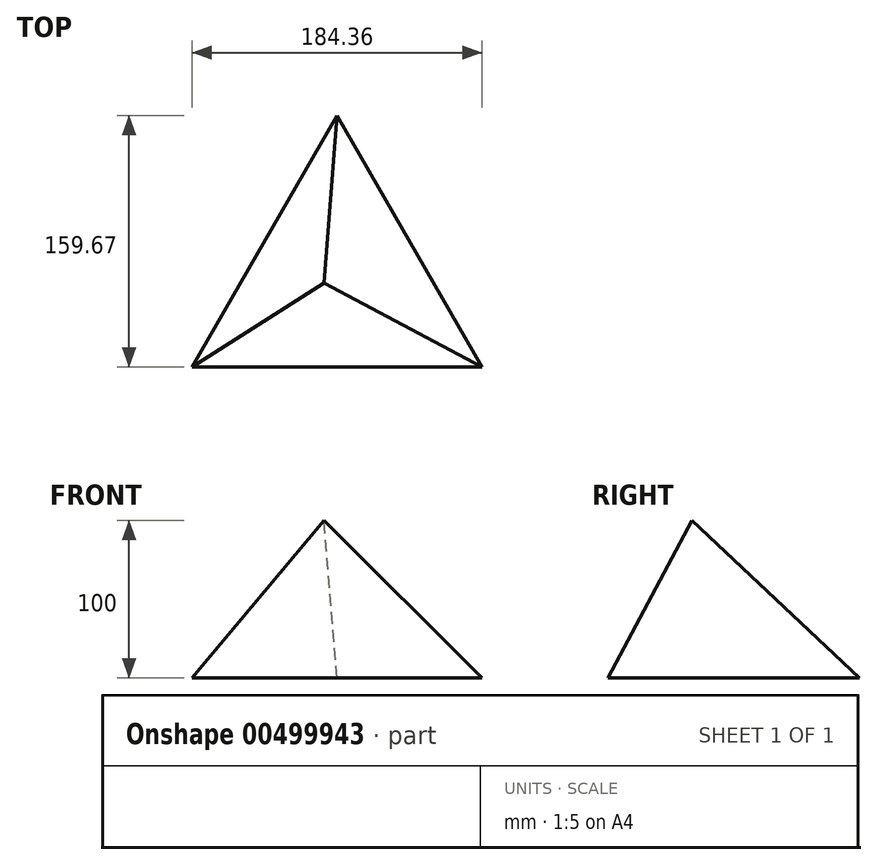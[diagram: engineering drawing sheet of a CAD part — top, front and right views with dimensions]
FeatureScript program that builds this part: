
annotation { "Feature Type Name" : "Feature", "Feature Type Description" : "" }
export const myFeature = defineFeature(function(context is Context, id is Id, definition is map)
    precondition{}
    {
        {
            var Q0;
            Q0=qCreatedBy(makeId("Top.planeOp"),FACE);
            var sketch = newSketch(context, id + "F0", { "sketchPlane" : qUnion([Q0])});
            skCircle(sketch, "E0.cCircle", {"center": v(0, 0) * mm, "radius": 106.45 * mm, "construction": true});
            skLineSegment(sketch, "E0.0", {"start": v(0, 106.45) * mm, "end": v(92.18, -53.22) * mm});
            skLineSegment(sketch, "E0.1", {"start": v(92.18, -53.22) * mm, "end": v(-92.18, -53.22) * mm});
            skLineSegment(sketch, "E0.2", {"start": v(-92.18, -53.22) * mm, "end": v(0, 106.45) * mm});
            skSolve(sketch);
        }
        {
            var Q0;
            Q0=qCreatedBy(makeId("Top.planeOp"),FACE);
            cPlane(context, id + "F1", {"entities" : qUnion([Q0]), "cplaneType" : CPlaneType.OFFSET, "offset" : 100 * mm, "width" : 150 * mm, "height" : 150 * mm});
        }
        {
            var Q0;
            Q0=qCreatedBy(id+"F1.planeOp",FACE);
            var sketch = newSketch(context, id + "F2", { "sketchPlane" : qUnion([Q0])});
            skPoint(sketch, "E1", {"position": v(-8.28, 0) * mm});
            skSolve(sketch);
        }
        {
            var Q0;
            Q0=makeQuery(id+"F0.imprint","IMPRINT",FACE,{"disambiguationData":[TD([[makeQuery(id+"F0.imprint","IMPRINT",EDGE,{"derivedFrom":sQuery(id+"F0.wireOp",EDGE,"E0.0")}),-1.0]])]});
            var Q1;
            Q1=sQuery(id+"F2.wireOp",VERTEX,"E1");
            loft(context, id + "F3", {"sheetProfilesArray" : [{ "sheetProfileEntities" : qUnion([Q0]) }, { "sheetProfileEntities" : qUnion([Q1]) }]});
        }
    });
